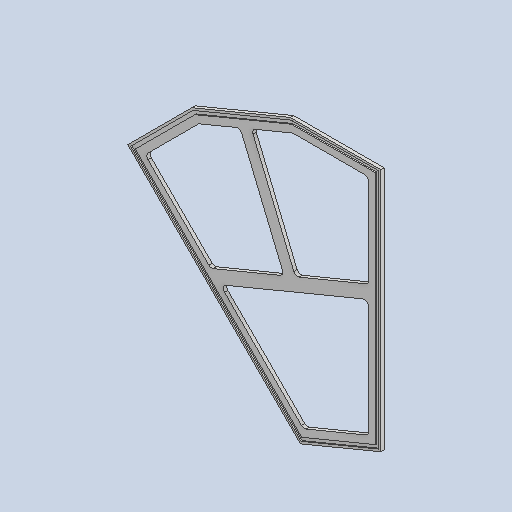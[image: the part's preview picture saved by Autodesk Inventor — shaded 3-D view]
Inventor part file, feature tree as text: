
AUTODESK INVENTOR PART (.ipt)
format: ipt  version: 2025 (Build 290162010, 162A)  size: 192,512 bytes
history: native  units: mm
features: extrude x3, fillet x3, sketch x3
ambient origin geometry x8: Origin, YZ Plane, XZ Plane, XY Plane, X Axis, Y Axis, Z Axis, Center Point
bodies: Solid1 (feature_tree)
feature tree (9):
  extrude  "Extrusion1"  Depth=260.0mm
  extrude  "Extrusion2"  Depth=8.0mm TaperAngle=0.0deg
  fillet  "Fillet1"  Radius=15.0mm
  extrude  "Extrusion3"  Depth=280.0mm
  fillet  "Fillet3"  Radius=30.0mm
  fillet  "Fillet4"  Radius=30.0mm
  sketch  "Sketch1"  dims[d0=513.0mm d2=260.0mm]
  sketch  "Sketch2"  dims[d3=635.0mm d5=8.0mm d6=0.0mm d10=15.0mm]
  sketch  "Sketch4"  dims[d11=30.0mm d12=280.0mm d13=30.0mm d14=30.0mm d15=15.0mm d16=0.0mm d17=0.0mm d18=10.0mm d21=30.0mm d22=30.0mm d23=30.0mm d24=30.0mm d26=5.0mm d27=8.0mm d28=3.0mm d29=0.0mm d30=16.0mm d31=8.0mm]
